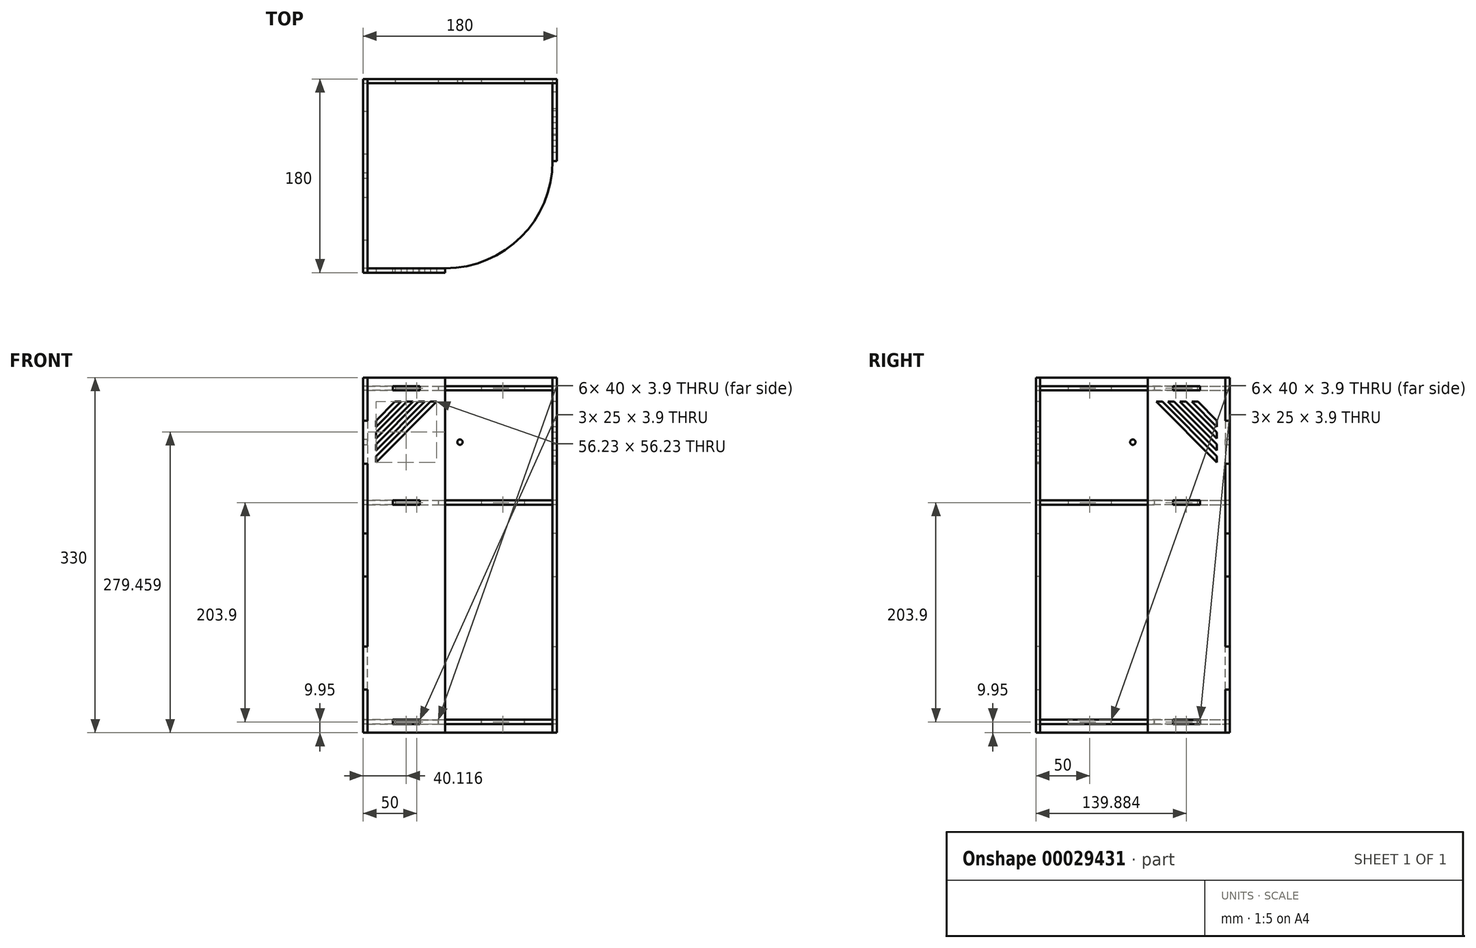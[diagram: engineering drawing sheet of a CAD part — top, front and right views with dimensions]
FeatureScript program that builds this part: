
annotation { "Feature Type Name" : "Feature", "Feature Type Description" : "" }
export const myFeature = defineFeature(function(context is Context, id is Id, definition is map)
    precondition{}
    {
        {
            var Q0;
            Q0=qCreatedBy(makeId("Right.planeOp"),FACE);
            var sketch = newSketch(context, id + "F0", { "sketchPlane" : qUnion([Q0])});
            skLineSegment(sketch, "E0.bottom", {"start": v(-90, 165) * mm, "end": v(90, 165) * mm});
            skLineSegment(sketch, "E0.top", {"start": v(-90, -165) * mm, "end": v(90, -165) * mm});
            skLineSegment(sketch, "E0.left", {"start": v(-90, 165) * mm, "end": v(-90, -165) * mm});
            skLineSegment(sketch, "E0.right", {"start": v(90, 165) * mm, "end": v(90, -165) * mm});
            skPoint(sketch, "E1", {"position": v(0, 165) * mm});
            skPoint(sketch, "E2", {"position": v(-90, 0) * mm});
            skLineSegment(sketch, "E3.bottom", {"start": v(-60, 157) * mm, "end": v(-20, 157) * mm});
            skLineSegment(sketch, "E3.top", {"start": v(-60, 153.1) * mm, "end": v(-20, 153.1) * mm});
            skLineSegment(sketch, "E3.left", {"start": v(-60, 157) * mm, "end": v(-60, 153.1) * mm});
            skLineSegment(sketch, "E3.right", {"start": v(-20, 157) * mm, "end": v(-20, 153.1) * mm});
            skLineSegment(sketch, "E4", {"start": v(0, 165) * mm, "end": v(0, -165) * mm, "construction": true});
            skLineSegment(sketch, "E5.MirrorCS", {"start": v(60, 157) * mm, "end": v(20, 157) * mm});
            skLineSegment(sketch, "E6.MirrorCS", {"start": v(60, 153.1) * mm, "end": v(20, 153.1) * mm});
            skLineSegment(sketch, "E7.MirrorCS", {"start": v(60, 157) * mm, "end": v(60, 153.1) * mm});
            skLineSegment(sketch, "E8.MirrorCS", {"start": v(20, 157) * mm, "end": v(20, 153.1) * mm});
            skLineSegment(sketch, "E9", {"start": v(-90, 0) * mm, "end": v(90, 0) * mm, "construction": true});
            skLineSegment(sketch, "E10.MirrorCS", {"start": v(-20, -157) * mm, "end": v(-20, -153.1) * mm});
            skLineSegment(sketch, "E11.MirrorCS", {"start": v(-60, -157) * mm, "end": v(-60, -153.1) * mm});
            skLineSegment(sketch, "E12.MirrorCS", {"start": v(-60, -153.1) * mm, "end": v(-20, -153.1) * mm});
            skLineSegment(sketch, "E13.MirrorCS", {"start": v(-60, -157) * mm, "end": v(-20, -157) * mm});
            skLineSegment(sketch, "E14.MirrorCS", {"start": v(60, -157) * mm, "end": v(20, -157) * mm});
            skLineSegment(sketch, "E15.MirrorCS", {"start": v(60, -153.1) * mm, "end": v(20, -153.1) * mm});
            skLineSegment(sketch, "E16.MirrorCS", {"start": v(60, -157) * mm, "end": v(60, -153.1) * mm});
            skLineSegment(sketch, "E17.MirrorCS", {"start": v(20, -157) * mm, "end": v(20, -153.1) * mm});
            skLineSegment(sketch, "E18", {"start": v(-90, 125) * mm, "end": v(-86, 125) * mm});
            skLineSegment(sketch, "E19", {"start": v(-86, 125) * mm, "end": v(-86, 85) * mm});
            skLineSegment(sketch, "E20", {"start": v(-86, 85) * mm, "end": v(-90, 85) * mm});
            skLineSegment(sketch, "E21", {"start": v(-90, 20) * mm, "end": v(-86, 20) * mm});
            skLineSegment(sketch, "E22", {"start": v(-86, 20) * mm, "end": v(-86, -20) * mm});
            skLineSegment(sketch, "E23", {"start": v(-86, -20) * mm, "end": v(-90, -20) * mm});
            skPoint(sketch, "E24", {"position": v(-86, 0) * mm});
            skLineSegment(sketch, "E25.MirrorCS", {"start": v(-90, -125) * mm, "end": v(-86, -125) * mm});
            skLineSegment(sketch, "E26.MirrorCS", {"start": v(-86, -85) * mm, "end": v(-90, -85) * mm});
            skLineSegment(sketch, "E27.MirrorCS", {"start": v(-86, -125) * mm, "end": v(-86, -85) * mm});
            skLineSegment(sketch, "E28.bottom", {"start": v(-60, 50.8) * mm, "end": v(-20, 50.8) * mm});
            skLineSegment(sketch, "E28.top", {"start": v(-60, 46.9) * mm, "end": v(-20, 46.9) * mm});
            skLineSegment(sketch, "E28.right", {"start": v(-20, 50.8) * mm, "end": v(-20, 46.9) * mm});
            skLineSegment(sketch, "E28.left", {"start": v(-60, 50.8) * mm, "end": v(-60, 46.9) * mm});
            skLineSegment(sketch, "E29.MirrorCS", {"start": v(20, 50.8) * mm, "end": v(20, 46.9) * mm});
            skLineSegment(sketch, "E30.MirrorCS", {"start": v(60, 50.8) * mm, "end": v(60, 46.9) * mm});
            skLineSegment(sketch, "E31.MirrorCS", {"start": v(60, 46.9) * mm, "end": v(20, 46.9) * mm});
            skLineSegment(sketch, "E32.MirrorCS", {"start": v(60, 50.8) * mm, "end": v(20, 50.8) * mm});
            skPoint(sketch, "E33.MirrorP", {"position": v(60, 0) * mm});
            skCircle(sketch, "E34", {"center": v(0, 105) * mm, "radius": 2.5 * mm});
            skPoint(sketch, "E35", {"position": v(-86, 105) * mm});
            skSolve(sketch);
        }
        {
            var Q0;
            {var subQ4=sQuery(id+"F0.wireOp",EDGE,"E0.bottom");Q0=makeQuery(id+"F0.imprint","IMPRINT",FACE,{"disambiguationData":[TD([[makeQuery(id+"F0.imprint","IMPRINT",EDGE,{"derivedFrom":subQ4}),-1.0]])]});}
            extrude(context, id + "F1", {"entities" : qUnion([Q0]), "depth" : 4 * mm});
        }
        {
            var Q0;
            Q0=makeQuery(id+"F1.opExtrude","SWEPT_BODY",BODY,{"disambiguationData":[OSD([sQuery(id+"F0.wireOp",EDGE,"E0.bottom"),sQuery(id+"F0.wireOp",EDGE,"E0.top"),sQuery(id+"F0.wireOp",EDGE,"E0.left"),sQuery(id+"F0.wireOp",EDGE,"E0.right"),sQuery(id+"F0.wireOp",EDGE,"E3.bottom"),sQuery(id+"F0.wireOp",EDGE,"E3.top"),sQuery(id+"F0.wireOp",EDGE,"E3.left"),sQuery(id+"F0.wireOp",EDGE,"E3.right"),sQuery(id+"F0.wireOp",EDGE,"E7.MirrorCS"),sQuery(id+"F0.wireOp",EDGE,"E8.MirrorCS"),sQuery(id+"F0.wireOp",EDGE,"E6.MirrorCS"),sQuery(id+"F0.wireOp",EDGE,"E5.MirrorCS"),sQuery(id+"F0.wireOp",EDGE,"E10.MirrorCS"),sQuery(id+"F0.wireOp",EDGE,"E11.MirrorCS"),sQuery(id+"F0.wireOp",EDGE,"E12.MirrorCS"),sQuery(id+"F0.wireOp",EDGE,"E13.MirrorCS"),sQuery(id+"F0.wireOp",EDGE,"E14.MirrorCS"),sQuery(id+"F0.wireOp",EDGE,"E17.MirrorCS"),sQuery(id+"F0.wireOp",EDGE,"E16.MirrorCS"),sQuery(id+"F0.wireOp",EDGE,"E15.MirrorCS"),sQuery(id+"F0.wireOp",EDGE,"E18"),sQuery(id+"F0.wireOp",EDGE,"E19"),sQuery(id+"F0.wireOp",EDGE,"E20"),sQuery(id+"F0.wireOp",EDGE,"E21"),sQuery(id+"F0.wireOp",EDGE,"E22"),sQuery(id+"F0.wireOp",EDGE,"E23"),sQuery(id+"F0.wireOp",EDGE,"E25.MirrorCS"),sQuery(id+"F0.wireOp",EDGE,"E26.MirrorCS"),sQuery(id+"F0.wireOp",EDGE,"E27.MirrorCS")])]});
            var Q1;
            Q1=makeQuery(id+"F1.opExtrude","CAP_EDGE",EDGE,{"disambiguationData":[OSD([sQuery(id+"F0.wireOp",EDGE,"E0.right")])],"isStart":true});
            transform(context, id + "F2", {"entities" : qUnion([Q0]), "transformType" : TransformType.ROTATION, "transformAxis" : qUnion([Q1]), "angle" : 90 * degree, "oppositeDirection" : true, "makeCopy" : true});
        }
        {
            var Q0;
            Q0=makeQuery(id+"F2.opPattern","COPY",BODY,{"derivedFrom":makeQuery(id+"F1.opExtrude","SWEPT_BODY",BODY,{"disambiguationData":[OSD([sQuery(id+"F0.wireOp",EDGE,"E0.bottom"),sQuery(id+"F0.wireOp",EDGE,"E0.top"),sQuery(id+"F0.wireOp",EDGE,"E0.left"),sQuery(id+"F0.wireOp",EDGE,"E0.right"),sQuery(id+"F0.wireOp",EDGE,"E3.bottom"),sQuery(id+"F0.wireOp",EDGE,"E3.top"),sQuery(id+"F0.wireOp",EDGE,"E3.left"),sQuery(id+"F0.wireOp",EDGE,"E3.right"),sQuery(id+"F0.wireOp",EDGE,"E7.MirrorCS"),sQuery(id+"F0.wireOp",EDGE,"E8.MirrorCS"),sQuery(id+"F0.wireOp",EDGE,"E6.MirrorCS"),sQuery(id+"F0.wireOp",EDGE,"E5.MirrorCS"),sQuery(id+"F0.wireOp",EDGE,"E10.MirrorCS"),sQuery(id+"F0.wireOp",EDGE,"E11.MirrorCS"),sQuery(id+"F0.wireOp",EDGE,"E12.MirrorCS"),sQuery(id+"F0.wireOp",EDGE,"E13.MirrorCS"),sQuery(id+"F0.wireOp",EDGE,"E14.MirrorCS"),sQuery(id+"F0.wireOp",EDGE,"E17.MirrorCS"),sQuery(id+"F0.wireOp",EDGE,"E16.MirrorCS"),sQuery(id+"F0.wireOp",EDGE,"E15.MirrorCS"),sQuery(id+"F0.wireOp",EDGE,"E18"),sQuery(id+"F0.wireOp",EDGE,"E19"),sQuery(id+"F0.wireOp",EDGE,"E20"),sQuery(id+"F0.wireOp",EDGE,"E21"),sQuery(id+"F0.wireOp",EDGE,"E22"),sQuery(id+"F0.wireOp",EDGE,"E23"),sQuery(id+"F0.wireOp",EDGE,"E25.MirrorCS"),sQuery(id+"F0.wireOp",EDGE,"E26.MirrorCS"),sQuery(id+"F0.wireOp",EDGE,"E27.MirrorCS")])]}),"instanceName":"1"});
            transform(context, id + "F3", {"entities" : qUnion([Q0]), "transformType" : TransformType.TRANSLATION_3D, "dx" : 0 * mm, "dy" : -4 * mm, "dz" : 0 * mm, "makeCopy" : false});
        }
        {
            var Q0;
            Q0=makeQuery(id+"F1.opExtrude","CAP_FACE",FACE,{"disambiguationData":[OSD([sQuery(id+"F0.wireOp",EDGE,"E0.bottom"),sQuery(id+"F0.wireOp",EDGE,"E0.top"),sQuery(id+"F0.wireOp",EDGE,"E0.left"),sQuery(id+"F0.wireOp",EDGE,"E0.right"),sQuery(id+"F0.wireOp",EDGE,"E3.bottom"),sQuery(id+"F0.wireOp",EDGE,"E3.top"),sQuery(id+"F0.wireOp",EDGE,"E3.left"),sQuery(id+"F0.wireOp",EDGE,"E3.right"),sQuery(id+"F0.wireOp",EDGE,"E7.MirrorCS"),sQuery(id+"F0.wireOp",EDGE,"E8.MirrorCS"),sQuery(id+"F0.wireOp",EDGE,"E6.MirrorCS"),sQuery(id+"F0.wireOp",EDGE,"E5.MirrorCS"),sQuery(id+"F0.wireOp",EDGE,"E10.MirrorCS"),sQuery(id+"F0.wireOp",EDGE,"E11.MirrorCS"),sQuery(id+"F0.wireOp",EDGE,"E12.MirrorCS"),sQuery(id+"F0.wireOp",EDGE,"E13.MirrorCS"),sQuery(id+"F0.wireOp",EDGE,"E14.MirrorCS"),sQuery(id+"F0.wireOp",EDGE,"E17.MirrorCS"),sQuery(id+"F0.wireOp",EDGE,"E16.MirrorCS"),sQuery(id+"F0.wireOp",EDGE,"E15.MirrorCS"),sQuery(id+"F0.wireOp",EDGE,"E18"),sQuery(id+"F0.wireOp",EDGE,"E19"),sQuery(id+"F0.wireOp",EDGE,"E20"),sQuery(id+"F0.wireOp",EDGE,"E21"),sQuery(id+"F0.wireOp",EDGE,"E22"),sQuery(id+"F0.wireOp",EDGE,"E23"),sQuery(id+"F0.wireOp",EDGE,"E25.MirrorCS"),sQuery(id+"F0.wireOp",EDGE,"E26.MirrorCS"),sQuery(id+"F0.wireOp",EDGE,"E27.MirrorCS")])],"isStart":false});
            var sketch = newSketch(context, id + "F4", { "sketchPlane" : qUnion([Q0])});
            skLineSegment(sketch, "E36", {"start": v(90, 125) * mm, "end": v(86, 125) * mm});
            skLineSegment(sketch, "E37", {"start": v(86, 125) * mm, "end": v(86, 85) * mm});
            skLineSegment(sketch, "E38", {"start": v(86, 85) * mm, "end": v(90, 85) * mm});
            skLineSegment(sketch, "E39", {"start": v(90, 125) * mm, "end": v(90, 85) * mm});
            skLineSegment(sketch, "E40.MirrorCS", {"start": v(90, -125) * mm, "end": v(90, -85) * mm});
            skLineSegment(sketch, "E41.MirrorCS", {"start": v(86, -85) * mm, "end": v(90, -85) * mm});
            skLineSegment(sketch, "E42.MirrorCS", {"start": v(86, -125) * mm, "end": v(86, -85) * mm});
            skLineSegment(sketch, "E43.MirrorCS", {"start": v(90, -125) * mm, "end": v(86, -125) * mm});
            skLineSegment(sketch, "E44.bottom", {"start": v(90, 20) * mm, "end": v(86, 20) * mm});
            skLineSegment(sketch, "E44.top", {"start": v(90, -20) * mm, "end": v(86, -20) * mm});
            skLineSegment(sketch, "E44.left", {"start": v(90, 20) * mm, "end": v(90, -20) * mm});
            skLineSegment(sketch, "E44.right", {"start": v(86, 20) * mm, "end": v(86, -20) * mm});
            skPoint(sketch, "E45", {"position": v(86, 0) * mm});
            skSolve(sketch);
        }
        {
            var Q0;
            Q0 = qSketchRegion(id + "F4", true);
            var Q1;
            Q1=makeQuery(id+"F1.opExtrude","CAP_FACE",FACE,{"disambiguationData":[OSD([sQuery(id+"F0.wireOp",EDGE,"E0.bottom"),sQuery(id+"F0.wireOp",EDGE,"E0.top"),sQuery(id+"F0.wireOp",EDGE,"E0.left"),sQuery(id+"F0.wireOp",EDGE,"E0.right"),sQuery(id+"F0.wireOp",EDGE,"E3.bottom"),sQuery(id+"F0.wireOp",EDGE,"E3.top"),sQuery(id+"F0.wireOp",EDGE,"E3.left"),sQuery(id+"F0.wireOp",EDGE,"E3.right"),sQuery(id+"F0.wireOp",EDGE,"E7.MirrorCS"),sQuery(id+"F0.wireOp",EDGE,"E8.MirrorCS"),sQuery(id+"F0.wireOp",EDGE,"E6.MirrorCS"),sQuery(id+"F0.wireOp",EDGE,"E5.MirrorCS"),sQuery(id+"F0.wireOp",EDGE,"E10.MirrorCS"),sQuery(id+"F0.wireOp",EDGE,"E11.MirrorCS"),sQuery(id+"F0.wireOp",EDGE,"E12.MirrorCS"),sQuery(id+"F0.wireOp",EDGE,"E13.MirrorCS"),sQuery(id+"F0.wireOp",EDGE,"E14.MirrorCS"),sQuery(id+"F0.wireOp",EDGE,"E17.MirrorCS"),sQuery(id+"F0.wireOp",EDGE,"E16.MirrorCS"),sQuery(id+"F0.wireOp",EDGE,"E15.MirrorCS"),sQuery(id+"F0.wireOp",EDGE,"E18"),sQuery(id+"F0.wireOp",EDGE,"E19"),sQuery(id+"F0.wireOp",EDGE,"E20"),sQuery(id+"F0.wireOp",EDGE,"E21"),sQuery(id+"F0.wireOp",EDGE,"E22"),sQuery(id+"F0.wireOp",EDGE,"E23"),sQuery(id+"F0.wireOp",EDGE,"E25.MirrorCS"),sQuery(id+"F0.wireOp",EDGE,"E26.MirrorCS"),sQuery(id+"F0.wireOp",EDGE,"E27.MirrorCS")])],"isStart":true});
            extrude(context, id + "F5", {"entities" : qUnion([Q0]), "operationType" : NewBodyOperationType.REMOVE, "endBound" : BoundingType.UP_TO_SURFACE, "oppositeDirection" : true, "endBoundEntityFace" : qUnion([Q1]), "depth" : 25 * mm});
        }
        {
            var Q0;
            Q0=makeQuery(id+"F1.opExtrude","SWEPT_BODY",BODY,{"disambiguationData":[OSD([sQuery(id+"F0.wireOp",EDGE,"E0.bottom"),sQuery(id+"F0.wireOp",EDGE,"E0.top"),sQuery(id+"F0.wireOp",EDGE,"E0.left"),sQuery(id+"F0.wireOp",EDGE,"E0.right"),sQuery(id+"F0.wireOp",EDGE,"E3.bottom"),sQuery(id+"F0.wireOp",EDGE,"E3.top"),sQuery(id+"F0.wireOp",EDGE,"E3.left"),sQuery(id+"F0.wireOp",EDGE,"E3.right"),sQuery(id+"F0.wireOp",EDGE,"E7.MirrorCS"),sQuery(id+"F0.wireOp",EDGE,"E8.MirrorCS"),sQuery(id+"F0.wireOp",EDGE,"E6.MirrorCS"),sQuery(id+"F0.wireOp",EDGE,"E5.MirrorCS"),sQuery(id+"F0.wireOp",EDGE,"E10.MirrorCS"),sQuery(id+"F0.wireOp",EDGE,"E11.MirrorCS"),sQuery(id+"F0.wireOp",EDGE,"E12.MirrorCS"),sQuery(id+"F0.wireOp",EDGE,"E13.MirrorCS"),sQuery(id+"F0.wireOp",EDGE,"E14.MirrorCS"),sQuery(id+"F0.wireOp",EDGE,"E17.MirrorCS"),sQuery(id+"F0.wireOp",EDGE,"E16.MirrorCS"),sQuery(id+"F0.wireOp",EDGE,"E15.MirrorCS"),sQuery(id+"F0.wireOp",EDGE,"E18"),sQuery(id+"F0.wireOp",EDGE,"E19"),sQuery(id+"F0.wireOp",EDGE,"E20"),sQuery(id+"F0.wireOp",EDGE,"E21"),sQuery(id+"F0.wireOp",EDGE,"E22"),sQuery(id+"F0.wireOp",EDGE,"E23"),sQuery(id+"F0.wireOp",EDGE,"E25.MirrorCS"),sQuery(id+"F0.wireOp",EDGE,"E26.MirrorCS"),sQuery(id+"F0.wireOp",EDGE,"E27.MirrorCS")])]});
            var Q1;
            Q1=makeQuery(id+"F2.opPattern","COPY",BODY,{"derivedFrom":makeQuery(id+"F1.opExtrude","SWEPT_BODY",BODY,{"disambiguationData":[OSD([sQuery(id+"F0.wireOp",EDGE,"E0.bottom"),sQuery(id+"F0.wireOp",EDGE,"E0.top"),sQuery(id+"F0.wireOp",EDGE,"E0.left"),sQuery(id+"F0.wireOp",EDGE,"E0.right"),sQuery(id+"F0.wireOp",EDGE,"E3.bottom"),sQuery(id+"F0.wireOp",EDGE,"E3.top"),sQuery(id+"F0.wireOp",EDGE,"E3.left"),sQuery(id+"F0.wireOp",EDGE,"E3.right"),sQuery(id+"F0.wireOp",EDGE,"E7.MirrorCS"),sQuery(id+"F0.wireOp",EDGE,"E8.MirrorCS"),sQuery(id+"F0.wireOp",EDGE,"E6.MirrorCS"),sQuery(id+"F0.wireOp",EDGE,"E5.MirrorCS"),sQuery(id+"F0.wireOp",EDGE,"E10.MirrorCS"),sQuery(id+"F0.wireOp",EDGE,"E11.MirrorCS"),sQuery(id+"F0.wireOp",EDGE,"E12.MirrorCS"),sQuery(id+"F0.wireOp",EDGE,"E13.MirrorCS"),sQuery(id+"F0.wireOp",EDGE,"E14.MirrorCS"),sQuery(id+"F0.wireOp",EDGE,"E17.MirrorCS"),sQuery(id+"F0.wireOp",EDGE,"E16.MirrorCS"),sQuery(id+"F0.wireOp",EDGE,"E15.MirrorCS"),sQuery(id+"F0.wireOp",EDGE,"E18"),sQuery(id+"F0.wireOp",EDGE,"E19"),sQuery(id+"F0.wireOp",EDGE,"E20"),sQuery(id+"F0.wireOp",EDGE,"E21"),sQuery(id+"F0.wireOp",EDGE,"E22"),sQuery(id+"F0.wireOp",EDGE,"E23"),sQuery(id+"F0.wireOp",EDGE,"E25.MirrorCS"),sQuery(id+"F0.wireOp",EDGE,"E26.MirrorCS"),sQuery(id+"F0.wireOp",EDGE,"E27.MirrorCS")])]}),"instanceName":"1"});
            booleanBodies(context, id + "F6", {"operationType" : BooleanOperationType.SUBTRACTION, "tools" : qUnion([Q0]), "targets" : qUnion([Q1]), "keepTools" : true});
        }
        {
            var Q0;
            {var subQ0=sQuery(id+"F0.wireOp",EDGE,"E0.left");Q0=makeQuery(id+"F1.opExtrude","SWEPT_FACE",FACE,{"disambiguationData":[OSD([subQ0]),TDD([makeQuery(id+"F0.imprint","IMPRINT",EDGE,{"disambiguationData":[TD([[makeQuery(id+"F0.imprint","INTERSECT",VERTEX,{"derivedFrom":[sQuery(id+"F0.wireOp",EDGE,"E0.bottom"),subQ0]}),-1.0]])],"derivedFrom":subQ0})])]});}
            var sketch = newSketch(context, id + "F7", { "sketchPlane" : qUnion([Q0])});
            skPoint(sketch, "E46.1", {"position": v(0, 165) * mm});
            skPoint(sketch, "E46.2", {"position": v(0, -165) * mm});
            skLineSegment(sketch, "E47", {"start": v(0, 165) * mm, "end": v(0, -165) * mm});
            skLineSegment(sketch, "E48", {"start": v(0, 165) * mm, "end": v(4, 165) * mm});
            skLineSegment(sketch, "E49", {"start": v(76.23, 165) * mm, "end": v(76.23, -165) * mm});
            skLineSegment(sketch, "E50", {"start": v(76.23, -165) * mm, "end": v(0, -165) * mm});
            skLineSegment(sketch, "E51.0", {"start": v(4, -125) * mm, "end": v(0, -125) * mm});
            skLineSegment(sketch, "E51.1", {"start": v(0, -125) * mm, "end": v(0, -85) * mm});
            skLineSegment(sketch, "E51.2", {"start": v(4, -125) * mm, "end": v(4, -85) * mm});
            skLineSegment(sketch, "E51.3", {"start": v(4, -85) * mm, "end": v(0, -85) * mm});
            skLineSegment(sketch, "E51.4", {"start": v(0, 20) * mm, "end": v(0, -20) * mm});
            skLineSegment(sketch, "E51.5", {"start": v(4, 20) * mm, "end": v(4, -20) * mm});
            skLineSegment(sketch, "E51.6", {"start": v(4, 20) * mm, "end": v(0, 20) * mm});
            skLineSegment(sketch, "E51.7", {"start": v(4, -20) * mm, "end": v(0, -20) * mm});
            skLineSegment(sketch, "E51.8", {"start": v(4, 85) * mm, "end": v(0, 85) * mm});
            skLineSegment(sketch, "E51.9", {"start": v(0, 125) * mm, "end": v(0, 85) * mm});
            skLineSegment(sketch, "E51.10", {"start": v(4, 125) * mm, "end": v(4, 85) * mm});
            skLineSegment(sketch, "E51.11", {"start": v(4, 125) * mm, "end": v(0, 125) * mm});
            skLineSegment(sketch, "E52", {"start": v(4, -20) * mm, "end": v(4, -85) * mm});
            skLineSegment(sketch, "E53", {"start": v(4, -125) * mm, "end": v(4, -165) * mm});
            skLineSegment(sketch, "E54", {"start": v(4, 20) * mm, "end": v(4, 85) * mm});
            skLineSegment(sketch, "E55", {"start": v(4, 125) * mm, "end": v(4, 165) * mm});
            skLineSegment(sketch, "E56", {"start": v(12, 125) * mm, "end": v(29.57, 142.57) * mm});
            skLineSegment(sketch, "E57", {"start": v(29.57, 142.57) * mm, "end": v(35.23, 142.57) * mm});
            skLineSegment(sketch, "E58", {"start": v(35.23, 142.57) * mm, "end": v(12, 119.34) * mm});
            skLineSegment(sketch, "E59", {"start": v(12, 119.34) * mm, "end": v(12, 125) * mm});
            skLineSegment(sketch, "E60.1.0.0", {"start": v(40.57, 142.57) * mm, "end": v(46.23, 142.57) * mm});
            skLineSegment(sketch, "E60.2.0.0", {"start": v(51.57, 142.57) * mm, "end": v(57.23, 142.57) * mm});
            skLineSegment(sketch, "E60.3.0.0", {"start": v(62.57, 142.57) * mm, "end": v(68.23, 142.57) * mm});
            skLineSegment(sketch, "E60.direction1", {"start": v(29.57, 142.57) * mm, "end": v(40.57, 142.57) * mm, "construction": true});
            skLineSegment(sketch, "E61.0.1.0", {"start": v(12, 108.34) * mm, "end": v(12, 114) * mm});
            skLineSegment(sketch, "E61.0.2.0", {"start": v(12, 97.34) * mm, "end": v(12, 103) * mm});
            skLineSegment(sketch, "E61.0.3.0", {"start": v(12, 86.34) * mm, "end": v(12, 92) * mm});
            skLineSegment(sketch, "E61.direction1", {"start": v(12, 119.34) * mm, "end": v(37, 119.34) * mm, "construction": true});
            skLineSegment(sketch, "E61.direction2", {"start": v(12, 119.34) * mm, "end": v(12, 108.34) * mm, "construction": true});
            skLineSegment(sketch, "E62", {"start": v(12, 114) * mm, "end": v(40.57, 142.57) * mm});
            skLineSegment(sketch, "E63", {"start": v(12, 108.34) * mm, "end": v(46.23, 142.57) * mm});
            skLineSegment(sketch, "E64", {"start": v(12, 103) * mm, "end": v(51.57, 142.57) * mm});
            skLineSegment(sketch, "E65", {"start": v(12, 97.34) * mm, "end": v(57.23, 142.57) * mm});
            skLineSegment(sketch, "E66", {"start": v(12, 92) * mm, "end": v(62.57, 142.57) * mm});
            skLineSegment(sketch, "E67", {"start": v(12, 86.34) * mm, "end": v(68.23, 142.57) * mm});
            skPoint(sketch, "E68.0", {"position": v(70, 157) * mm});
            skPoint(sketch, "E68.1", {"position": v(70, 153.1) * mm});
            skPoint(sketch, "E68.2", {"position": v(70, 50.8) * mm});
            skPoint(sketch, "E68.3", {"position": v(70, 46.9) * mm});
            skPoint(sketch, "E68.4", {"position": v(70, -153.1) * mm});
            skPoint(sketch, "E68.5", {"position": v(70, -157) * mm});
            skLineSegment(sketch, "E69.bottom", {"start": v(27.62, 157) * mm, "end": v(52.62, 157) * mm});
            skLineSegment(sketch, "E69.top", {"start": v(27.62, 153.1) * mm, "end": v(52.62, 153.1) * mm});
            skLineSegment(sketch, "E69.left", {"start": v(27.62, 157) * mm, "end": v(27.62, 153.1) * mm});
            skLineSegment(sketch, "E69.right", {"start": v(52.62, 157) * mm, "end": v(52.62, 153.1) * mm});
            skLineSegment(sketch, "E70.bottom", {"start": v(27.62, 50.8) * mm, "end": v(52.62, 50.8) * mm});
            skLineSegment(sketch, "E70.top", {"start": v(27.62, 46.9) * mm, "end": v(52.62, 46.9) * mm});
            skLineSegment(sketch, "E70.left", {"start": v(27.62, 50.8) * mm, "end": v(27.62, 46.9) * mm});
            skLineSegment(sketch, "E70.right", {"start": v(52.62, 50.8) * mm, "end": v(52.62, 46.9) * mm});
            skLineSegment(sketch, "E71.bottom", {"start": v(27.62, -153.1) * mm, "end": v(52.62, -153.1) * mm});
            skLineSegment(sketch, "E71.top", {"start": v(27.62, -157) * mm, "end": v(52.62, -157) * mm});
            skLineSegment(sketch, "E71.left", {"start": v(27.62, -153.1) * mm, "end": v(27.62, -157) * mm});
            skLineSegment(sketch, "E71.right", {"start": v(52.62, -153.1) * mm, "end": v(52.62, -157) * mm});
            skLineSegment(sketch, "E72", {"start": v(4, 165) * mm, "end": v(76.23, 165) * mm});
            skPoint(sketch, "E73", {"position": v(40.12, 165) * mm});
            skPoint(sketch, "E74", {"position": v(40.12, 157) * mm});
            skSolve(sketch);
        }
        {
            var Q0;
            Q0=makeQuery(id+"F7.imprint","IMPRINT",FACE,{"disambiguationData":[TD([[makeQuery(id+"F7.imprint","IMPRINT",EDGE,{"derivedFrom":sQuery(id+"F7.wireOp",EDGE,"E51.8")}),-1.0]])]});
            var Q1;
            {var subQ3=sQuery(id+"F7.wireOp",EDGE,"E49");Q1=makeQuery(id+"F7.imprint","IMPRINT",FACE,{"disambiguationData":[TD([[makeQuery(id+"F7.imprint","IMPRINT",EDGE,{"derivedFrom":subQ3}),-1.0]])]});}
            var Q2;
            Q2=makeQuery(id+"F7.imprint","IMPRINT",FACE,{"disambiguationData":[TD([[makeQuery(id+"F7.imprint","IMPRINT",EDGE,{"derivedFrom":sQuery(id+"F7.wireOp",EDGE,"E51.4")}),1.0]])]});
            var Q3;
            Q3=makeQuery(id+"F7.imprint","IMPRINT",FACE,{"disambiguationData":[TD([[makeQuery(id+"F7.imprint","IMPRINT",EDGE,{"derivedFrom":sQuery(id+"F7.wireOp",EDGE,"E51.0")}),-1.0]])]});
            extrude(context, id + "F8", {"entities" : qUnion([Q0, Q1, Q2, Q3]), "oppositeDirection" : true, "depth" : 4 * mm});
        }
        {
            var Q0;
            Q0=makeQuery(id+"F8.opExtrude","SWEPT_BODY",BODY,{"disambiguationData":[OSD([sQuery(id+"F7.wireOp",EDGE,"E48"),sQuery(id+"F7.wireOp",EDGE,"E49"),sQuery(id+"F7.wireOp",EDGE,"E50"),sQuery(id+"F7.wireOp",EDGE,"E51.0"),sQuery(id+"F7.wireOp",EDGE,"E51.1"),sQuery(id+"F7.wireOp",EDGE,"E51.3"),sQuery(id+"F7.wireOp",EDGE,"E51.4"),sQuery(id+"F7.wireOp",EDGE,"E51.6"),sQuery(id+"F7.wireOp",EDGE,"E51.7"),sQuery(id+"F7.wireOp",EDGE,"E51.8"),sQuery(id+"F7.wireOp",EDGE,"E51.9"),sQuery(id+"F7.wireOp",EDGE,"E51.11"),sQuery(id+"F7.wireOp",EDGE,"E52"),sQuery(id+"F7.wireOp",EDGE,"E53"),sQuery(id+"F7.wireOp",EDGE,"E54"),sQuery(id+"F7.wireOp",EDGE,"E55"),sQuery(id+"F7.wireOp",EDGE,"27fb87be-ac01-425a-b387-c8e02b68969a.0"),sQuery(id+"F7.wireOp",EDGE,"27fb87be-ac01-425a-b387-c8e02b68969a.1"),sQuery(id+"F7.wireOp",EDGE,"27fb87be-ac01-425a-b387-c8e02b68969a.2"),sQuery(id+"F7.wireOp",EDGE,"27fb87be-ac01-425a-b387-c8e02b68969a.3"),sQuery(id+"F7.wireOp",EDGE,"27fb87be-ac01-425a-b387-c8e02b68969a.4"),sQuery(id+"F7.wireOp",EDGE,"27fb87be-ac01-425a-b387-c8e02b68969a.5"),sQuery(id+"F7.wireOp",EDGE,"27fb87be-ac01-425a-b387-c8e02b68969a.6"),sQuery(id+"F7.wireOp",EDGE,"27fb87be-ac01-425a-b387-c8e02b68969a.7"),sQuery(id+"F7.wireOp",EDGE,"27fb87be-ac01-425a-b387-c8e02b68969a.8"),sQuery(id+"F7.wireOp",EDGE,"27fb87be-ac01-425a-b387-c8e02b68969a.9"),sQuery(id+"F7.wireOp",EDGE,"27fb87be-ac01-425a-b387-c8e02b68969a.10"),sQuery(id+"F7.wireOp",EDGE,"27fb87be-ac01-425a-b387-c8e02b68969a.11")])]});
            var Q1;
            Q1=makeQuery(id+"F1.opExtrude","CAP_VERTEX",VERTEX,{"disambiguationData":[OSD([sQuery(id+"F0.wireOp",EDGE,"E0.left"),sQuery(id+"F0.wireOp",EDGE,"E18")])],"isStart":true});
            var Q2;
            Q2=makeQuery(id+"F2.opPattern","COPY",VERTEX,{"derivedFrom":makeQuery(id+"F1.opExtrude","CAP_VERTEX",VERTEX,{"disambiguationData":[OSD([sQuery(id+"F0.wireOp",EDGE,"E18"),sQuery(id+"F0.wireOp",EDGE,"E19")])],"isStart":false}),"instanceName":"1"});
            transform(context, id + "F9", {"entities" : qUnion([Q0]), "transformType" : TransformType.TRANSLATION_ENTITY, "oppositeDirectionEntity" : false, "transformLine" : qUnion([Q1, Q2]), "makeCopy" : true});
        }
        {
            var Q0;
            Q0=makeQuery(id+"F9.opPattern","COPY",BODY,{"derivedFrom":makeQuery(id+"F8.opExtrude","SWEPT_BODY",BODY,{"disambiguationData":[OSD([sQuery(id+"F7.wireOp",EDGE,"E48"),sQuery(id+"F7.wireOp",EDGE,"E49"),sQuery(id+"F7.wireOp",EDGE,"E50"),sQuery(id+"F7.wireOp",EDGE,"E51.0"),sQuery(id+"F7.wireOp",EDGE,"E51.1"),sQuery(id+"F7.wireOp",EDGE,"E51.3"),sQuery(id+"F7.wireOp",EDGE,"E51.4"),sQuery(id+"F7.wireOp",EDGE,"E51.6"),sQuery(id+"F7.wireOp",EDGE,"E51.7"),sQuery(id+"F7.wireOp",EDGE,"E51.8"),sQuery(id+"F7.wireOp",EDGE,"E51.9"),sQuery(id+"F7.wireOp",EDGE,"E51.11"),sQuery(id+"F7.wireOp",EDGE,"E52"),sQuery(id+"F7.wireOp",EDGE,"E53"),sQuery(id+"F7.wireOp",EDGE,"E54"),sQuery(id+"F7.wireOp",EDGE,"E55"),sQuery(id+"F7.wireOp",EDGE,"27fb87be-ac01-425a-b387-c8e02b68969a.0"),sQuery(id+"F7.wireOp",EDGE,"27fb87be-ac01-425a-b387-c8e02b68969a.1"),sQuery(id+"F7.wireOp",EDGE,"27fb87be-ac01-425a-b387-c8e02b68969a.2"),sQuery(id+"F7.wireOp",EDGE,"27fb87be-ac01-425a-b387-c8e02b68969a.3"),sQuery(id+"F7.wireOp",EDGE,"27fb87be-ac01-425a-b387-c8e02b68969a.4"),sQuery(id+"F7.wireOp",EDGE,"27fb87be-ac01-425a-b387-c8e02b68969a.5"),sQuery(id+"F7.wireOp",EDGE,"27fb87be-ac01-425a-b387-c8e02b68969a.6"),sQuery(id+"F7.wireOp",EDGE,"27fb87be-ac01-425a-b387-c8e02b68969a.7"),sQuery(id+"F7.wireOp",EDGE,"27fb87be-ac01-425a-b387-c8e02b68969a.8"),sQuery(id+"F7.wireOp",EDGE,"27fb87be-ac01-425a-b387-c8e02b68969a.9"),sQuery(id+"F7.wireOp",EDGE,"27fb87be-ac01-425a-b387-c8e02b68969a.10"),sQuery(id+"F7.wireOp",EDGE,"27fb87be-ac01-425a-b387-c8e02b68969a.11")])]}),"instanceName":"1"});
            var Q1;
            Q1=makeQuery(id+"F2.opPattern","COPY",EDGE,{"derivedFrom":makeQuery(id+"F1.opExtrude","CAP_EDGE",EDGE,{"disambiguationData":[OSD([sQuery(id+"F0.wireOp",EDGE,"E19")])],"isStart":false}),"instanceName":"1"});
            transform(context, id + "F10", {"entities" : qUnion([Q0]), "transformType" : TransformType.ROTATION, "transformAxis" : qUnion([Q1]), "angle" : 90 * degree, "makeCopy" : false});
        }
        {
            var Q0;
            Q0=makeQuery(id+"F2.opPattern","COPY",FACE,{"derivedFrom":makeQuery(id+"F1.opExtrude","SWEPT_FACE",FACE,{"disambiguationData":[OSD([sQuery(id+"F0.wireOp",EDGE,"E6.MirrorCS")])]}),"instanceName":"1"});
            var sketch = newSketch(context, id + "F11", { "sketchPlane" : qUnion([Q0])});
            skLineSegment(sketch, "E75", {"start": v(0, -90) * mm, "end": v(0, 90) * mm});
            skLineSegment(sketch, "E76", {"start": v(0, 90) * mm, "end": v(180, 90) * mm});
            skPoint(sketch, "E77.0", {"position": v(0, -90) * mm});
            skPoint(sketch, "E78.1", {"position": v(180, 90) * mm});
            skPoint(sketch, "E79.0", {"position": v(4, -60) * mm});
            skPoint(sketch, "E79.1", {"position": v(4, -20) * mm});
            skPoint(sketch, "E79.2", {"position": v(4, 20) * mm});
            skPoint(sketch, "E79.3", {"position": v(4, 60) * mm});
            skPoint(sketch, "E79.4", {"position": v(30, 86) * mm});
            skPoint(sketch, "E79.5", {"position": v(70, 86) * mm});
            skPoint(sketch, "E79.6", {"position": v(110, 86) * mm});
            skPoint(sketch, "E79.7", {"position": v(150, 86) * mm});
            skLineSegment(sketch, "E80", {"start": v(4, -60) * mm, "end": v(0, -60) * mm});
            skLineSegment(sketch, "E81", {"start": v(0, -60) * mm, "end": v(0, -20) * mm});
            skLineSegment(sketch, "E82", {"start": v(0, -20) * mm, "end": v(4, -20) * mm});
            skLineSegment(sketch, "E83", {"start": v(4, 20) * mm, "end": v(0, 20) * mm});
            skLineSegment(sketch, "E84", {"start": v(0, 20) * mm, "end": v(0, 60) * mm});
            skLineSegment(sketch, "E85", {"start": v(0, 60) * mm, "end": v(4, 60) * mm});
            skLineSegment(sketch, "E86", {"start": v(70, 86) * mm, "end": v(70, 90) * mm});
            skLineSegment(sketch, "E87", {"start": v(70, 90) * mm, "end": v(30, 90) * mm});
            skLineSegment(sketch, "E88", {"start": v(30, 90) * mm, "end": v(30, 86) * mm});
            skLineSegment(sketch, "E89", {"start": v(150, 86) * mm, "end": v(150, 90) * mm});
            skLineSegment(sketch, "E90", {"start": v(150, 90) * mm, "end": v(110, 90) * mm});
            skLineSegment(sketch, "E91", {"start": v(110, 90) * mm, "end": v(110, 86) * mm});
            skLineSegment(sketch, "E92", {"start": v(4, 60) * mm, "end": v(4, 86) * mm});
            skLineSegment(sketch, "E93", {"start": v(4, 86) * mm, "end": v(30, 86) * mm});
            skLineSegment(sketch, "E94", {"start": v(4, -20) * mm, "end": v(4, 20) * mm});
            skLineSegment(sketch, "E95", {"start": v(70, 86) * mm, "end": v(110, 86) * mm});
            skLineSegment(sketch, "E96", {"start": v(27.62, -90) * mm, "end": v(27.62, -86) * mm});
            skLineSegment(sketch, "E97", {"start": v(27.62, -86) * mm, "end": v(4, -86) * mm});
            skLineSegment(sketch, "E98", {"start": v(52.62, -90) * mm, "end": v(52.62, -86) * mm});
            skLineSegment(sketch, "E99", {"start": v(52.62, -86) * mm, "end": v(76.23, -86) * mm});
            skLineSegment(sketch, "E100", {"start": v(180, 62.38) * mm, "end": v(176, 62.38) * mm});
            skLineSegment(sketch, "E101", {"start": v(180, 37.38) * mm, "end": v(176, 37.38) * mm});
            skLineSegment(sketch, "E102", {"start": v(176, 37.38) * mm, "end": v(176, 13.77) * mm});
            skArc(sketch, "E103", {"start": v(76.23, -86) * mm, "mid": v(146.78, -56.78) * mm, "end": v(176, 13.77) * mm});
            skPoint(sketch, "E104.0", {"position": v(76.23, -86) * mm});
            skLineSegment(sketch, "E105", {"start": v(27.62, -90) * mm, "end": v(52.62, -90) * mm});
            skLineSegment(sketch, "E106", {"start": v(4, -60) * mm, "end": v(4, -86) * mm});
            skPoint(sketch, "E107", {"position": v(40.12, -90) * mm});
            skLineSegment(sketch, "E108", {"start": v(176, 62.38) * mm, "end": v(176, 86) * mm});
            skLineSegment(sketch, "E109", {"start": v(176, 86) * mm, "end": v(150, 86) * mm});
            skLineSegment(sketch, "E110", {"start": v(180, 37.38) * mm, "end": v(180, 62.38) * mm});
            skPoint(sketch, "E111", {"position": v(180, 49.88) * mm});
            skLineSegment(sketch, "E112.0", {"start": v(176, 86) * mm, "end": v(176, 13.77) * mm});
            skPoint(sketch, "E113", {"position": v(176, 49.88) * mm});
            skLineSegment(sketch, "E114.0", {"start": v(4, -86) * mm, "end": v(76.23, -86) * mm});
            skPoint(sketch, "E115", {"position": v(40.12, -86) * mm});
            skSolve(sketch);
        }
        {
            var Q0;
            {var subQ7=sQuery(id+"F11.wireOp",EDGE,"E80");Q0=makeQuery(id+"F11.imprint","IMPRINT",FACE,{"disambiguationData":[TD([[makeQuery(id+"F11.imprint","IMPRINT",EDGE,{"derivedFrom":subQ7}),-1.0]])]});}
            var Q1;
            Q1=makeQuery(id+"F11.imprint","IMPRINT",FACE,{"disambiguationData":[TD([[makeQuery(id+"F11.imprint","IMPRINT",EDGE,{"derivedFrom":sQuery(id+"F11.wireOp",EDGE,"E86")}),-1.0]])]});
            var Q2;
            {var subQ2=sQuery(id+"F11.wireOp",EDGE,"E96");Q2=makeQuery(id+"F11.imprint","IMPRINT",FACE,{"disambiguationData":[TD([[makeQuery(id+"F11.imprint","IMPRINT",EDGE,{"derivedFrom":subQ2}),-1.0]])]});}
            var Q3;
            {var subQ2=sQuery(id+"F11.wireOp",EDGE,"E100");Q3=makeQuery(id+"F11.imprint","IMPRINT",FACE,{"disambiguationData":[TD([[makeQuery(id+"F11.imprint","IMPRINT",EDGE,{"derivedFrom":subQ2}),1.0]])]});}
            extrude(context, id + "F12", {"entities" : qUnion([Q0, Q1, Q2, Q3]), "depth" : 4 * mm});
        }
        {
            var Q0;
            Q0=makeQuery(id+"F12.opExtrude","SWEPT_BODY",BODY,{"disambiguationData":[OSD([sQuery(id+"F11.wireOp",EDGE,"25e4b00e-3c9e-4ac6-a40b-53ce5d611315"),sQuery(id+"F11.wireOp",EDGE,"4142476f-a2ea-496c-8985-60285c6aa32e"),sQuery(id+"F11.wireOp",EDGE,"521145a3-1eaf-437f-8093-aa1492a88572"),sQuery(id+"F11.wireOp",EDGE,"E80"),sQuery(id+"F11.wireOp",EDGE,"E81"),sQuery(id+"F11.wireOp",EDGE,"E82"),sQuery(id+"F11.wireOp",EDGE,"E83"),sQuery(id+"F11.wireOp",EDGE,"E84"),sQuery(id+"F11.wireOp",EDGE,"E85"),sQuery(id+"F11.wireOp",EDGE,"E86"),sQuery(id+"F11.wireOp",EDGE,"E87"),sQuery(id+"F11.wireOp",EDGE,"E88"),sQuery(id+"F11.wireOp",EDGE,"E89"),sQuery(id+"F11.wireOp",EDGE,"E90"),sQuery(id+"F11.wireOp",EDGE,"E91"),sQuery(id+"F11.wireOp",EDGE,"E92"),sQuery(id+"F11.wireOp",EDGE,"E93"),sQuery(id+"F11.wireOp",EDGE,"E94"),sQuery(id+"F11.wireOp",EDGE,"0d5f376d-ae6c-41e0-9e16-ab8bf266952a"),sQuery(id+"F11.wireOp",EDGE,"E95"),sQuery(id+"F11.wireOp",EDGE,"3c4746e5-74c6-4d19-b3ec-d284e9314dd8")])]});
            var Q1;
            Q1=makeQuery(id+"F1.opExtrude","CAP_VERTEX",VERTEX,{"disambiguationData":[OSD([sQuery(id+"F0.wireOp",EDGE,"E3.top"),sQuery(id+"F0.wireOp",EDGE,"E3.right")])],"isStart":true});
            var Q2;
            Q2=makeQuery(id+"F1.opExtrude","CAP_VERTEX",VERTEX,{"disambiguationData":[OSD([sQuery(id+"F0.wireOp",EDGE,"E28.top"),sQuery(id+"F0.wireOp",EDGE,"E28.right")])],"isStart":true});
            transform(context, id + "F13", {"entities" : qUnion([Q0]), "transformType" : TransformType.TRANSLATION_ENTITY, "oppositeDirectionEntity" : false, "transformLine" : qUnion([Q1, Q2]), "makeCopy" : true});
        }
        {
            var Q0;
            Q0=makeQuery(id+"F13.opPattern","COPY",BODY,{"derivedFrom":makeQuery(id+"F12.opExtrude","SWEPT_BODY",BODY,{"disambiguationData":[OSD([sQuery(id+"F11.wireOp",EDGE,"25e4b00e-3c9e-4ac6-a40b-53ce5d611315"),sQuery(id+"F11.wireOp",EDGE,"4142476f-a2ea-496c-8985-60285c6aa32e"),sQuery(id+"F11.wireOp",EDGE,"521145a3-1eaf-437f-8093-aa1492a88572"),sQuery(id+"F11.wireOp",EDGE,"E80"),sQuery(id+"F11.wireOp",EDGE,"E81"),sQuery(id+"F11.wireOp",EDGE,"E82"),sQuery(id+"F11.wireOp",EDGE,"E83"),sQuery(id+"F11.wireOp",EDGE,"E84"),sQuery(id+"F11.wireOp",EDGE,"E85"),sQuery(id+"F11.wireOp",EDGE,"E86"),sQuery(id+"F11.wireOp",EDGE,"E87"),sQuery(id+"F11.wireOp",EDGE,"E88"),sQuery(id+"F11.wireOp",EDGE,"E89"),sQuery(id+"F11.wireOp",EDGE,"E90"),sQuery(id+"F11.wireOp",EDGE,"E91"),sQuery(id+"F11.wireOp",EDGE,"E92"),sQuery(id+"F11.wireOp",EDGE,"E93"),sQuery(id+"F11.wireOp",EDGE,"E94"),sQuery(id+"F11.wireOp",EDGE,"0d5f376d-ae6c-41e0-9e16-ab8bf266952a"),sQuery(id+"F11.wireOp",EDGE,"E95"),sQuery(id+"F11.wireOp",EDGE,"3c4746e5-74c6-4d19-b3ec-d284e9314dd8")])]}),"instanceName":"1"});
            var Q1;
            Q1=makeQuery(id+"F1.opExtrude","CAP_VERTEX",VERTEX,{"disambiguationData":[OSD([sQuery(id+"F0.wireOp",EDGE,"E28.top"),sQuery(id+"F0.wireOp",EDGE,"E28.left")])],"isStart":true});
            var Q2;
            Q2=makeQuery(id+"F1.opExtrude","CAP_VERTEX",VERTEX,{"disambiguationData":[OSD([sQuery(id+"F0.wireOp",EDGE,"E11.MirrorCS"),sQuery(id+"F0.wireOp",EDGE,"E13.MirrorCS")])],"isStart":true});
            transform(context, id + "F14", {"entities" : qUnion([Q0]), "transformType" : TransformType.TRANSLATION_ENTITY, "oppositeDirectionEntity" : false, "transformLine" : qUnion([Q1, Q2]), "makeCopy" : true});
        }
    });
